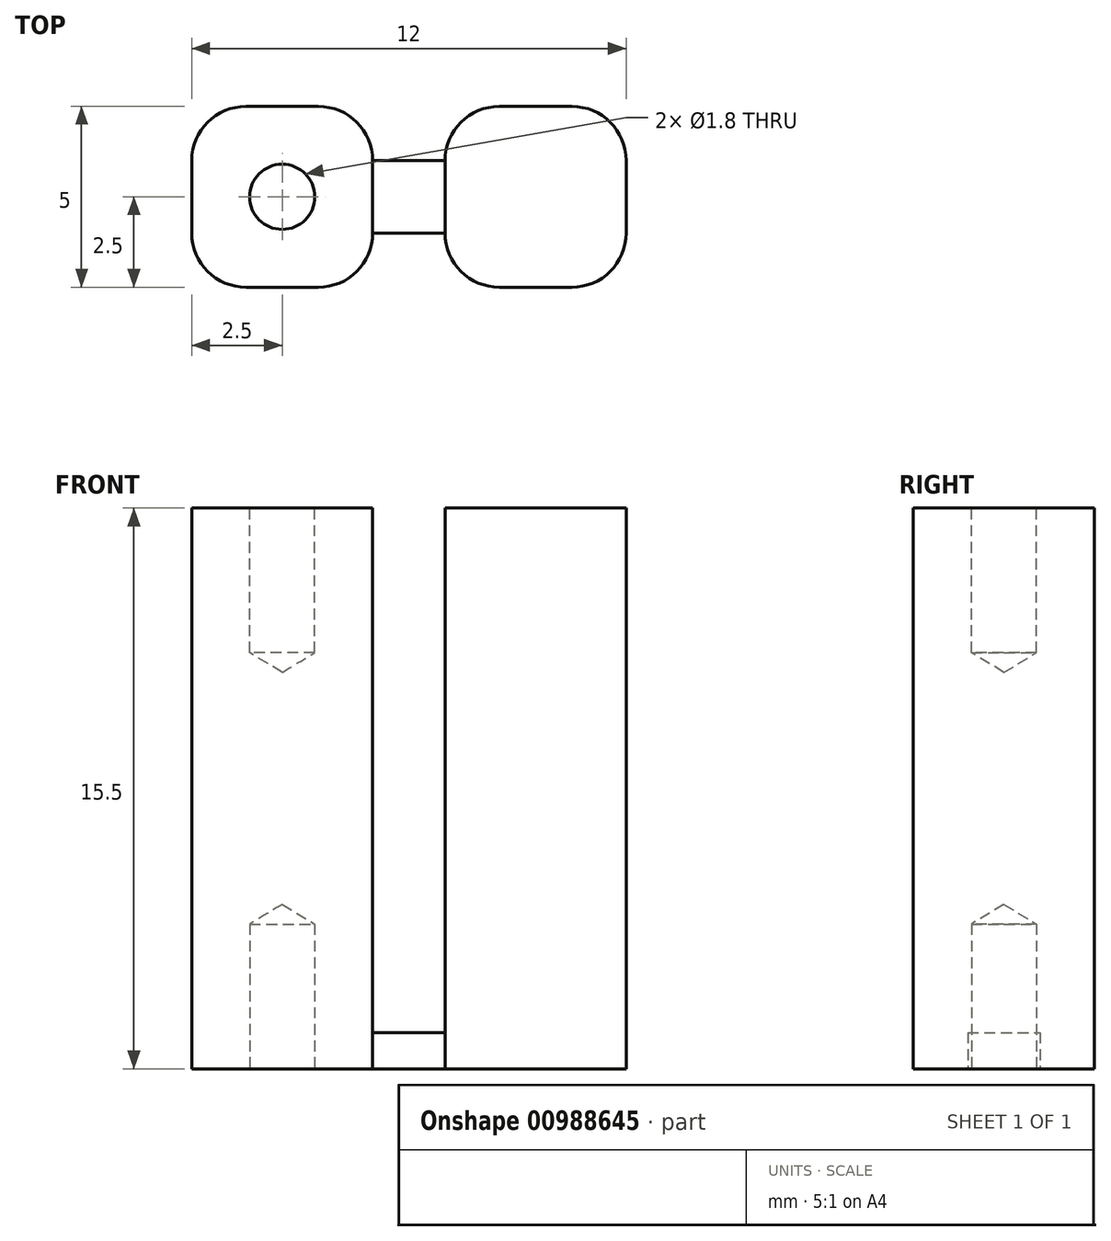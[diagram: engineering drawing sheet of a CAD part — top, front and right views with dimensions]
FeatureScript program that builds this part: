
annotation { "Feature Type Name" : "Feature", "Feature Type Description" : "" }
export const myFeature = defineFeature(function(context is Context, id is Id, definition is map)
    precondition{}
    {
        {
            var Q0;
            Q0=qCreatedBy(makeId("Top.planeOp"),FACE);
            var sketch = newSketch(context, id + "F0", { "sketchPlane" : qUnion([Q0])});
            skLineSegment(sketch, "E0.bottom", {"start": v(1, -2.5) * mm, "end": v(-1, -2.5) * mm});
            skLineSegment(sketch, "E0.top", {"start": v(1, 2.5) * mm, "end": v(-1, 2.5) * mm});
            skLineSegment(sketch, "E0.left", {"start": v(2.5, -1) * mm, "end": v(2.5, 1) * mm});
            skLineSegment(sketch, "E0.right", {"start": v(-2.5, -1) * mm, "end": v(-2.5, 1) * mm});
            skPoint(sketch, "E0.middle", {"position": v(0, 0) * mm});
            skPoint(sketch, "E1.visualSharp", {"position": v(-2.5, 2.5) * mm});
            skArc(sketch, "E1.filletArc", {"start": v(-1, 2.5) * mm, "mid": v(-2.06, 2.06) * mm, "end": v(-2.5, 1) * mm});
            skPoint(sketch, "E2.visualSharp", {"position": v(2.5, 2.5) * mm});
            skArc(sketch, "E2.filletArc", {"start": v(2.5, 1) * mm, "mid": v(2.06, 2.06) * mm, "end": v(1, 2.5) * mm});
            skPoint(sketch, "E3.visualSharp", {"position": v(-2.5, -2.5) * mm});
            skArc(sketch, "E3.filletArc", {"start": v(-2.5, -1) * mm, "mid": v(-2.06, -2.06) * mm, "end": v(-1, -2.5) * mm});
            skPoint(sketch, "E4.visualSharp", {"position": v(2.5, -2.5) * mm});
            skArc(sketch, "E4.filletArc", {"start": v(1, -2.5) * mm, "mid": v(2.06, -2.06) * mm, "end": v(2.5, -1) * mm});
            skLineSegment(sketch, "E5", {"start": v(2.5, 1) * mm, "end": v(3.5, 1) * mm});
            skLineSegment(sketch, "E6", {"start": v(2.5, -1) * mm, "end": v(3.5, -1) * mm});
            skLineSegment(sketch, "E7.MirrorCS", {"start": v(4.5, -1) * mm, "end": v(4.5, 1) * mm});
            skArc(sketch, "E8.MirrorCS", {"start": v(4.5, 1) * mm, "mid": v(4.94, 2.06) * mm, "end": v(6, 2.5) * mm});
            skLineSegment(sketch, "E9.MirrorCS", {"start": v(6, 2.5) * mm, "end": v(8, 2.5) * mm});
            skArc(sketch, "E10.MirrorCS", {"start": v(8, 2.5) * mm, "mid": v(9.06, 2.06) * mm, "end": v(9.5, 1) * mm});
            skLineSegment(sketch, "E11.MirrorCS", {"start": v(9.5, -1) * mm, "end": v(9.5, 1) * mm});
            skArc(sketch, "E12.MirrorCS", {"start": v(9.5, -1) * mm, "mid": v(9.06, -2.06) * mm, "end": v(8, -2.5) * mm});
            skLineSegment(sketch, "E13.MirrorCS", {"start": v(6, -2.5) * mm, "end": v(8, -2.5) * mm});
            skArc(sketch, "E14.MirrorCS", {"start": v(6, -2.5) * mm, "mid": v(4.94, -2.06) * mm, "end": v(4.5, -1) * mm});
            skLineSegment(sketch, "E15.MirrorCS", {"start": v(4.5, 1) * mm, "end": v(3.5, 1) * mm});
            skLineSegment(sketch, "E16.MirrorCS", {"start": v(4.5, -1) * mm, "end": v(3.5, -1) * mm});
            skPoint(sketch, "E17.MirrorP", {"position": v(7, 0) * mm});
            skSolve(sketch);
        }
        {
            var Q0;
            Q0=makeQuery(id+"F0.imprint","IMPRINT",FACE,{"disambiguationData":[TD([[makeQuery(id+"F0.imprint","IMPRINT",EDGE,{"derivedFrom":sQuery(id+"F0.wireOp",EDGE,"E0.bottom")}),-1.0]])]});
            var Q1;
            Q1=makeQuery(id+"F0.imprint","IMPRINT",FACE,{"disambiguationData":[TD([[makeQuery(id+"F0.imprint","IMPRINT",EDGE,{"derivedFrom":sQuery(id+"F0.wireOp",EDGE,"E7.MirrorCS")}),-1.0]])]});
            extrude(context, id + "F1", {"entities" : qUnion([Q0, Q1]), "depth" : 15.5 * mm, "offsetDistance" : 25 * mm});
        }
        {
            var Q0;
            Q0=makeQuery(id+"F0.imprint","IMPRINT",FACE,{"disambiguationData":[TD([[makeQuery(id+"F0.imprint","IMPRINT",EDGE,{"derivedFrom":sQuery(id+"F0.wireOp",EDGE,"E0.left")}),-1.0]])]});
            extrude(context, id + "F2", {"entities" : qUnion([Q0]), "depth" : 1 * mm, "offsetDistance" : 25 * mm});
        }
        {
            var Q0;
            Q0=makeQuery(id+"F1.opExtrude","CAP_FACE",FACE,{"disambiguationData":[OSD([sQuery(id+"F0.wireOp",EDGE,"E0.bottom"),sQuery(id+"F0.wireOp",EDGE,"E0.top"),sQuery(id+"F0.wireOp",EDGE,"E0.left"),sQuery(id+"F0.wireOp",EDGE,"E0.right"),sQuery(id+"F0.wireOp",EDGE,"E1.filletArc"),sQuery(id+"F0.wireOp",EDGE,"E2.filletArc"),sQuery(id+"F0.wireOp",EDGE,"E3.filletArc"),sQuery(id+"F0.wireOp",EDGE,"E4.filletArc")])],"isStart":false});
            var sketch = newSketch(context, id + "F3", { "sketchPlane" : qUnion([Q0])});
            skPoint(sketch, "E18", {"position": v(0, 0) * mm});
            skLineSegment(sketch, "E19", {"start": v(0, 0) * mm, "end": v(7, 0) * mm});
            skPoint(sketch, "E20", {"position": v(7, 0) * mm});
            skSolve(sketch);
        }
        {
            var Q0;
            Q0=sQuery(id+"F3.wireOp",VERTEX,"E18");
            var Q1;
            Q1=sQuery(id+"F3.wireOp",VERTEX,"E20");
            var Q2;
            Q2=makeQuery(id+"F1.opExtrude","SWEPT_BODY",BODY,{"disambiguationData":[OSD([sQuery(id+"F0.wireOp",EDGE,"E0.bottom"),sQuery(id+"F0.wireOp",EDGE,"E0.top"),sQuery(id+"F0.wireOp",EDGE,"E0.left"),sQuery(id+"F0.wireOp",EDGE,"E0.right"),sQuery(id+"F0.wireOp",EDGE,"E1.filletArc"),sQuery(id+"F0.wireOp",EDGE,"E2.filletArc"),sQuery(id+"F0.wireOp",EDGE,"E3.filletArc"),sQuery(id+"F0.wireOp",EDGE,"E4.filletArc")])]});
            hole(context, id + "F4", {"style" : HoleStyle.SIMPLE, "endStyle" : HoleEndStyle.BLIND, "holeDiameter" : 1.8 * mm, "majorDiameter" : 5 * mm, "holeDepth" : 4 * mm, "isTappedThrough" : true, "tappedDepth" : 12 * mm, "tapClearance" : 3, "startFromSketch" : true, "locations" : qUnion([Q0, Q1]), "scope" : qUnion([Q2])});
        }
        {
            var Q0;
            Q0=sQuery(id+"F0.wireOp",VERTEX,"E17.MirrorP");
            var Q1;
            Q1=sQuery(id+"F0.wireOp",VERTEX,"E0.middle");
            var Q2;
            Q2=makeQuery(id+"F1.opExtrude","SWEPT_BODY",BODY,{"disambiguationData":[OSD([sQuery(id+"F0.wireOp",EDGE,"E0.bottom"),sQuery(id+"F0.wireOp",EDGE,"E0.top"),sQuery(id+"F0.wireOp",EDGE,"E0.left"),sQuery(id+"F0.wireOp",EDGE,"E0.right"),sQuery(id+"F0.wireOp",EDGE,"E1.filletArc"),sQuery(id+"F0.wireOp",EDGE,"E2.filletArc"),sQuery(id+"F0.wireOp",EDGE,"E3.filletArc"),sQuery(id+"F0.wireOp",EDGE,"E4.filletArc")])]});
            hole(context, id + "F5", {"style" : HoleStyle.SIMPLE, "endStyle" : HoleEndStyle.BLIND, "oppositeDirection" : true, "holeDiameter" : 1.8 * mm, "majorDiameter" : 5 * mm, "holeDepth" : 4 * mm, "isTappedThrough" : true, "tappedDepth" : 12 * mm, "tapClearance" : 3, "startFromSketch" : true, "locations" : qUnion([Q0, Q1]), "scope" : qUnion([Q2])});
        }
    });
